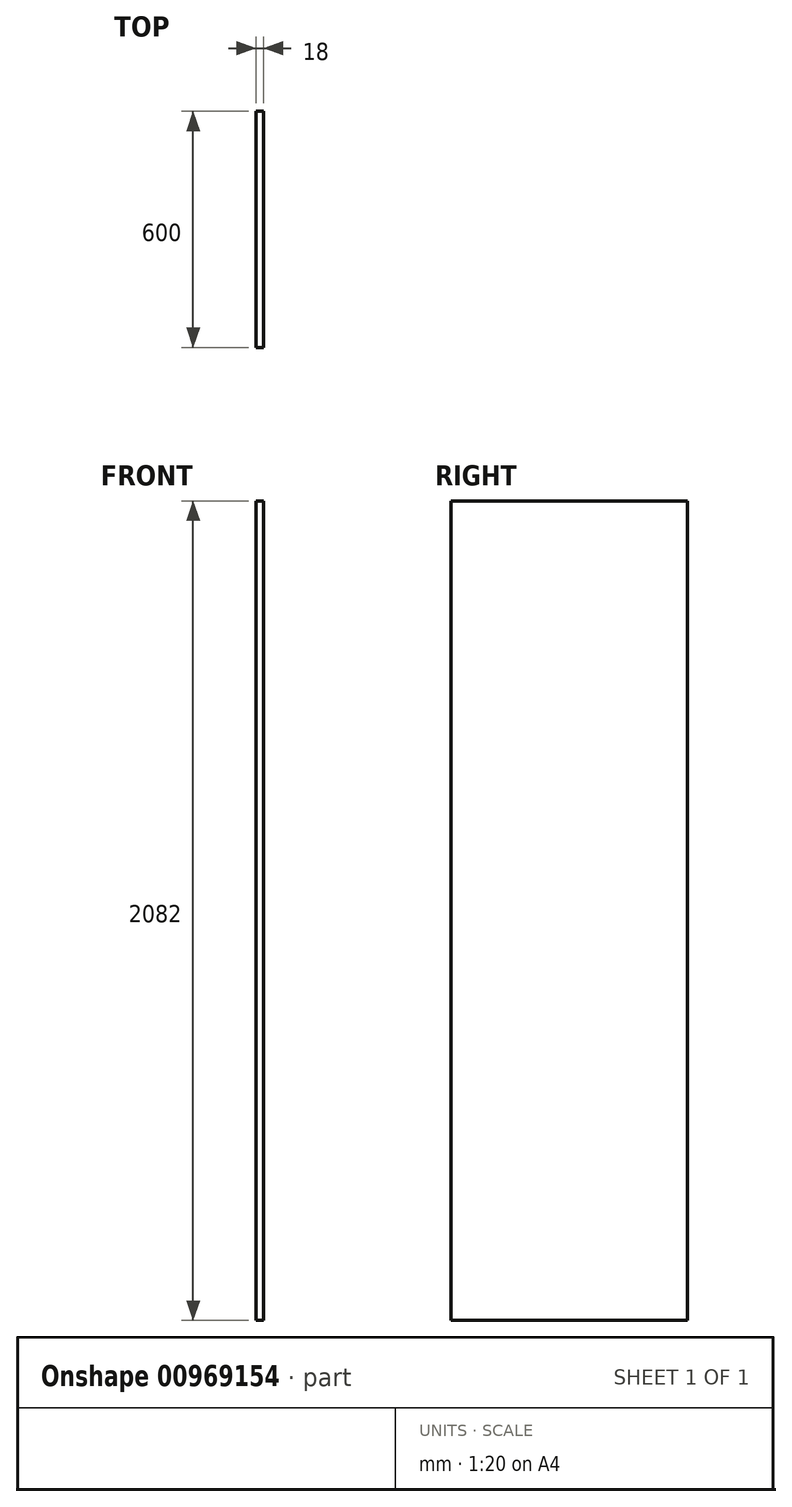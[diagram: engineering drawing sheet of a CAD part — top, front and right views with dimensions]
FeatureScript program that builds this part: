
annotation { "Feature Type Name" : "Feature", "Feature Type Description" : "" }
export const myFeature = defineFeature(function(context is Context, id is Id, definition is map)
    precondition{}
    {
        {
            var Q0;
            Q0=qCreatedBy(makeId("Right.planeOp"),FACE);
            var sketch = newSketch(context, id + "F0", { "sketchPlane" : qUnion([Q0])});
            skLineSegment(sketch, "E0.bottom", {"start": v(0, 0) * mm, "end": v(600, 0) * mm});
            skLineSegment(sketch, "E0.top", {"start": v(0, 2082) * mm, "end": v(600, 2082) * mm});
            skLineSegment(sketch, "E0.left", {"start": v(0, 0) * mm, "end": v(0, 2082) * mm});
            skLineSegment(sketch, "E0.right", {"start": v(600, 0) * mm, "end": v(600, 2082) * mm});
            skSolve(sketch);
        }
        {
            var Q0;
            Q0 = qSketchRegion(id + "F0", true);
            extrude(context, id + "F1", {"entities" : qUnion([Q0]), "depth" : 18 * mm, "offsetDistance" : 25 * mm});
        }
        {
            var Q0;
            Q0=makeQuery(id+"F1.opExtrude","SWEPT_BODY",BODY,{"disambiguationData":[OSD([sQuery(id+"F0.wireOp",EDGE,"E0.bottom"),sQuery(id+"F0.wireOp",EDGE,"E0.top"),sQuery(id+"F0.wireOp",EDGE,"E0.left"),sQuery(id+"F0.wireOp",EDGE,"E0.right")])]});
            transform(context, id + "F2", {"entities" : qUnion([Q0]), "transformType" : TransformType.TRANSLATION_3D, "dx" : 0 * mm, "dy" : 0 * mm, "dz" : 0 * mm, "makeCopy" : true});
        }
    });
